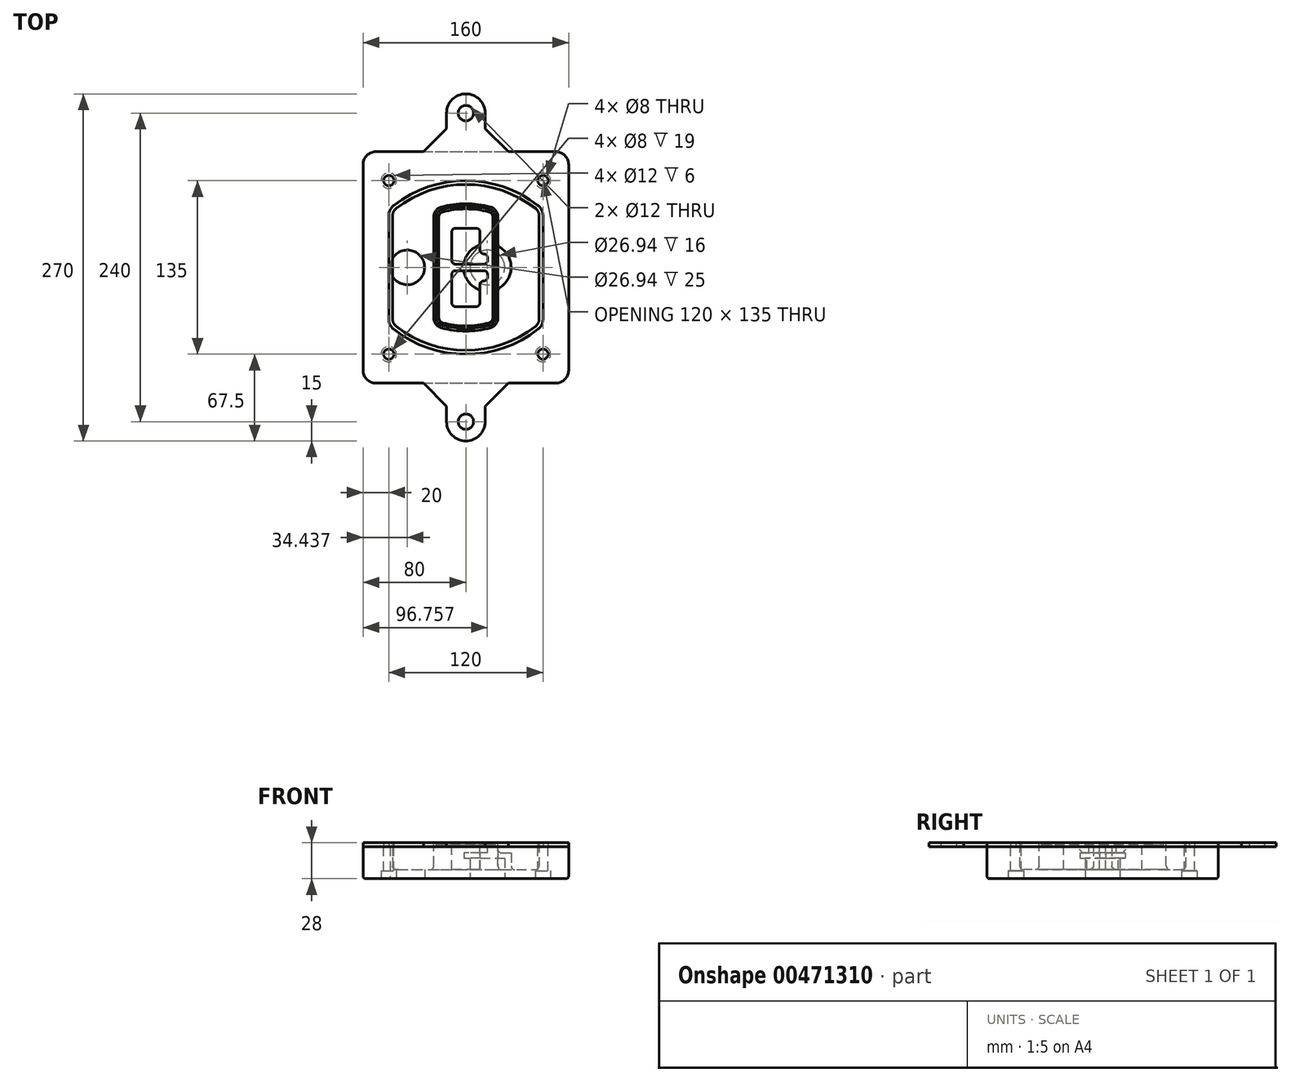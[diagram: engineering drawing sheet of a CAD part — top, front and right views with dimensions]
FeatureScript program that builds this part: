
annotation { "Feature Type Name" : "Feature", "Feature Type Description" : "" }
export const myFeature = defineFeature(function(context is Context, id is Id, definition is map)
    precondition{}
    {
        {
            var Q0;
            Q0=qCreatedBy(makeId("Top.planeOp"),FACE);
            var sketch = newSketch(context, id + "F0", { "sketchPlane" : qUnion([Q0])});
            skPoint(sketch, "E0.rect.middle", {"position": v(0, 0) * mm});
            skLineSegment(sketch, "E1.bottom", {"start": v(-70, -90) * mm, "end": v(70, -90) * mm});
            skLineSegment(sketch, "E1.top", {"start": v(-70, 90) * mm, "end": v(70, 90) * mm});
            skLineSegment(sketch, "E1.left", {"start": v(-80, -80) * mm, "end": v(-80, 80) * mm});
            skLineSegment(sketch, "E1.right", {"start": v(80, -80) * mm, "end": v(80, 80) * mm});
            skLineSegment(sketch, "E2", {"start": v(-80, 90) * mm, "end": v(80, -90) * mm, "construction": true});
            skLineSegment(sketch, "E3", {"start": v(80, 90) * mm, "end": v(-80, -90) * mm, "construction": true});
            skCircle(sketch, "E4", {"center": v(-60, 67.5) * mm, "radius": 4 * mm});
            skCircle(sketch, "E5", {"center": v(60, 67.5) * mm, "radius": 4 * mm});
            skCircle(sketch, "E6", {"center": v(60, -67.5) * mm, "radius": 4 * mm});
            skCircle(sketch, "E7", {"center": v(-60, -67.5) * mm, "radius": 4 * mm});
            skLineSegment(sketch, "E8", {"start": v(-60, 67.5) * mm, "end": v(60, 67.5) * mm, "construction": true});
            skLineSegment(sketch, "E9", {"start": v(60, 67.5) * mm, "end": v(60, -67.5) * mm, "construction": true});
            skLineSegment(sketch, "E10", {"start": v(60, -67.5) * mm, "end": v(-60, -67.5) * mm, "construction": true});
            skLineSegment(sketch, "E11", {"start": v(-60, -67.5) * mm, "end": v(-60, 67.5) * mm, "construction": true});
            skLineSegment(sketch, "E12", {"start": v(-60, 40.3) * mm, "end": v(-60, -40.3) * mm});
            skLineSegment(sketch, "E13", {"start": v(60, 40.3) * mm, "end": v(60, -40.3) * mm});
            skArc(sketch, "E14", {"start": v(56.15, 48.18) * mm, "mid": v(0, 67.5) * mm, "end": v(-56.15, 48.18) * mm});
            skArc(sketch, "E15", {"start": v(-56.15, -48.18) * mm, "mid": v(0, -67.5) * mm, "end": v(56.15, -48.18) * mm});
            skLineSegment(sketch, "E16", {"start": v(-60, 0) * mm, "end": v(60, 0) * mm, "construction": true});
            skPoint(sketch, "E17.visualSharp", {"position": v(-60, -45) * mm});
            skArc(sketch, "E17.filletArc", {"start": v(-60, -40.3) * mm, "mid": v(-58.99, -44.68) * mm, "end": v(-56.15, -48.18) * mm});
            skPoint(sketch, "E18.visualSharp", {"position": v(-60, 45) * mm});
            skArc(sketch, "E18.filletArc", {"start": v(-56.15, 48.18) * mm, "mid": v(-58.99, 44.68) * mm, "end": v(-60, 40.3) * mm});
            skPoint(sketch, "E19.visualSharp", {"position": v(60, 45) * mm});
            skArc(sketch, "E19.filletArc", {"start": v(60, 40.3) * mm, "mid": v(58.99, 44.68) * mm, "end": v(56.15, 48.18) * mm});
            skPoint(sketch, "E20.visualSharp", {"position": v(60, -45) * mm});
            skArc(sketch, "E20.filletArc", {"start": v(56.15, -48.18) * mm, "mid": v(58.99, -44.68) * mm, "end": v(60, -40.3) * mm});
            skPoint(sketch, "E21.visualSharp", {"position": v(-80, 90) * mm});
            skArc(sketch, "E21.filletArc", {"start": v(-70, 90) * mm, "mid": v(-77.07, 87.07) * mm, "end": v(-80, 80) * mm});
            skPoint(sketch, "E22.visualSharp", {"position": v(80, 90) * mm});
            skArc(sketch, "E22.filletArc", {"start": v(80, 80) * mm, "mid": v(77.07, 87.07) * mm, "end": v(70, 90) * mm});
            skPoint(sketch, "E23.visualSharp", {"position": v(80, -90) * mm});
            skArc(sketch, "E23.filletArc", {"start": v(70, -90) * mm, "mid": v(77.07, -87.07) * mm, "end": v(80, -80) * mm});
            skPoint(sketch, "E24.visualSharp", {"position": v(-80, -90) * mm});
            skArc(sketch, "E24.filletArc", {"start": v(-80, -80) * mm, "mid": v(-77.07, -87.07) * mm, "end": v(-70, -90) * mm});
            skArc(sketch, "E25.0", {"start": v(57, 40.3) * mm, "mid": v(56.3, 43.36) * mm, "end": v(54.3, 45.81) * mm});
            skLineSegment(sketch, "E25.1", {"start": v(57, 40.3) * mm, "end": v(57, -40.3) * mm});
            skArc(sketch, "E25.2", {"start": v(54.3, -45.81) * mm, "mid": v(56.3, -43.36) * mm, "end": v(57, -40.3) * mm});
            skArc(sketch, "E25.3", {"start": v(-54.3, -45.81) * mm, "mid": v(0, -64.5) * mm, "end": v(54.3, -45.81) * mm});
            skArc(sketch, "E25.4", {"start": v(-57, -40.3) * mm, "mid": v(-56.3, -43.36) * mm, "end": v(-54.3, -45.81) * mm});
            skArc(sketch, "E25.5", {"start": v(54.3, 45.81) * mm, "mid": v(0, 64.5) * mm, "end": v(-54.3, 45.81) * mm});
            skLineSegment(sketch, "E25.6", {"start": v(-57, 40.3) * mm, "end": v(-57, -40.3) * mm});
            skArc(sketch, "E25.7", {"start": v(-54.3, 45.81) * mm, "mid": v(-56.3, 43.36) * mm, "end": v(-57, 40.3) * mm});
            skArc(sketch, "E26.0", {"start": v(-58.62, 51.33) * mm, "mid": v(-62.58, 46.43) * mm, "end": v(-64, 40.3) * mm});
            skArc(sketch, "E26.1", {"start": v(58.62, 51.33) * mm, "mid": v(0, 71.5) * mm, "end": v(-58.62, 51.33) * mm});
            skArc(sketch, "E26.2", {"start": v(64, 40.3) * mm, "mid": v(62.58, 46.43) * mm, "end": v(58.62, 51.33) * mm});
            skLineSegment(sketch, "E26.3", {"start": v(64, 40.3) * mm, "end": v(64, -40.3) * mm});
            skArc(sketch, "E26.4", {"start": v(58.62, -51.33) * mm, "mid": v(62.58, -46.43) * mm, "end": v(64, -40.3) * mm});
            skLineSegment(sketch, "E26.5", {"start": v(-64, 40.3) * mm, "end": v(-64, -40.3) * mm});
            skArc(sketch, "E26.6", {"start": v(-58.62, -51.33) * mm, "mid": v(0, -71.5) * mm, "end": v(58.62, -51.33) * mm});
            skArc(sketch, "E26.7", {"start": v(-64, -40.3) * mm, "mid": v(-62.58, -46.43) * mm, "end": v(-58.62, -51.33) * mm});
            skSolve(sketch);
        }
        {
            var Q0;
            Q0=makeQuery(id+"F0.imprint","IMPRINT",FACE,{"disambiguationData":[TD([[makeQuery(id+"F0.imprint","IMPRINT",EDGE,{"derivedFrom":sQuery(id+"F0.wireOp",EDGE,"E1.bottom")}),1.0]])]});
            var Q1;
            Q1=makeQuery(id+"F0.imprint","IMPRINT",FACE,{"disambiguationData":[TD([[makeQuery(id+"F0.imprint","IMPRINT",EDGE,{"derivedFrom":sQuery(id+"F0.wireOp",EDGE,"E12")}),1.0]])]});
            var Q2;
            Q2=makeQuery(id+"F0.imprint","IMPRINT",FACE,{"disambiguationData":[TD([[makeQuery(id+"F0.imprint","IMPRINT",EDGE,{"derivedFrom":sQuery(id+"F0.wireOp",EDGE,"E25.0")}),1.0]])]});
            var Q3;
            Q3=makeQuery(id+"F0.imprint","IMPRINT",FACE,{"disambiguationData":[TD([[makeQuery(id+"F0.imprint","IMPRINT",EDGE,{"derivedFrom":sQuery(id+"F0.wireOp",EDGE,"E12")}),-1.0]])]});
            extrude(context, id + "F1", {"entities" : qUnion([Q0, Q1, Q2, Q3]), "oppositeDirection" : true, "depth" : 25 * mm});
        }
        {
            var Q0;
            Q0=makeQuery(id+"F0.imprint","IMPRINT",FACE,{"disambiguationData":[TD([[makeQuery(id+"F0.imprint","IMPRINT",EDGE,{"derivedFrom":sQuery(id+"F0.wireOp",EDGE,"E12")}),1.0]])]});
            extrude(context, id + "F2", {"entities" : qUnion([Q0]), "operationType" : NewBodyOperationType.ADD, "depth" : 3 * mm});
        }
        {
            var Q0;
            Q0=makeQuery(id+"F0.imprint","IMPRINT",FACE,{"disambiguationData":[TD([[makeQuery(id+"F0.imprint","IMPRINT",EDGE,{"derivedFrom":sQuery(id+"F0.wireOp",EDGE,"E25.0")}),1.0]])]});
            extrude(context, id + "F3", {"entities" : qUnion([Q0]), "operationType" : NewBodyOperationType.REMOVE, "oppositeDirection" : true, "depth" : 18 * mm});
        }
        {
            var Q0;
            Q0=makeQuery(id+"F2.opExtrude","CAP_FACE",FACE,{"disambiguationData":[OSD([sQuery(id+"F0.wireOp",EDGE,"E12"),sQuery(id+"F0.wireOp",EDGE,"E13"),sQuery(id+"F0.wireOp",EDGE,"E14"),sQuery(id+"F0.wireOp",EDGE,"E15"),sQuery(id+"F0.wireOp",EDGE,"E17.filletArc"),sQuery(id+"F0.wireOp",EDGE,"E18.filletArc"),sQuery(id+"F0.wireOp",EDGE,"E19.filletArc"),sQuery(id+"F0.wireOp",EDGE,"E20.filletArc"),sQuery(id+"F0.wireOp",EDGE,"E25.0"),sQuery(id+"F0.wireOp",EDGE,"E25.1"),sQuery(id+"F0.wireOp",EDGE,"E25.2"),sQuery(id+"F0.wireOp",EDGE,"E25.3"),sQuery(id+"F0.wireOp",EDGE,"E25.4"),sQuery(id+"F0.wireOp",EDGE,"E25.5"),sQuery(id+"F0.wireOp",EDGE,"E25.6"),sQuery(id+"F0.wireOp",EDGE,"E25.7")])],"isStart":false});
            var sketch = newSketch(context, id + "F4", { "sketchPlane" : qUnion([Q0])});
            skArc(sketch, "E27.0", {"start": v(-19.08, -46.97) * mm, "mid": v(0, -49.5) * mm, "end": v(19.08, -46.97) * mm});
            skArc(sketch, "E28.0", {"start": v(19.08, 46.97) * mm, "mid": v(0, 49.5) * mm, "end": v(-19.08, 46.97) * mm});
            skLineSegment(sketch, "E29", {"start": v(-25, 39.25) * mm, "end": v(-25, -39.25) * mm});
            skLineSegment(sketch, "E30", {"start": v(25, 39.25) * mm, "end": v(25, -39.25) * mm});
            skLineSegment(sketch, "E31", {"start": v(-25, 45.1) * mm, "end": v(25, 45.1) * mm, "construction": true});
            skLineSegment(sketch, "E32", {"start": v(-25, -45.1) * mm, "end": v(25, -45.1) * mm, "construction": true});
            skPoint(sketch, "E33.visualSharp", {"position": v(-25, 45.1) * mm});
            skArc(sketch, "E33.filletArc", {"start": v(-19.08, 46.97) * mm, "mid": v(-23.35, 44.11) * mm, "end": v(-25, 39.25) * mm});
            skPoint(sketch, "E34.visualSharp", {"position": v(25, 45.1) * mm});
            skArc(sketch, "E34.filletArc", {"start": v(25, 39.25) * mm, "mid": v(23.35, 44.11) * mm, "end": v(19.08, 46.97) * mm});
            skPoint(sketch, "E35.visualSharp", {"position": v(25, -45.1) * mm});
            skArc(sketch, "E35.filletArc", {"start": v(19.08, -46.97) * mm, "mid": v(23.35, -44.11) * mm, "end": v(25, -39.25) * mm});
            skPoint(sketch, "E36.visualSharp", {"position": v(-25, -45.1) * mm});
            skArc(sketch, "E36.filletArc", {"start": v(-25, -39.25) * mm, "mid": v(-23.35, -44.11) * mm, "end": v(-19.08, -46.97) * mm});
            skArc(sketch, "E37.0", {"start": v(54.3, 45.81) * mm, "mid": v(0, 64.5) * mm, "end": v(-54.3, 45.81) * mm});
            skArc(sketch, "E37.1", {"start": v(-54.3, 45.81) * mm, "mid": v(-56.3, 43.36) * mm, "end": v(-57, 40.3) * mm});
            skLineSegment(sketch, "E37.2", {"start": v(-57, 40.3) * mm, "end": v(-57, -40.3) * mm});
            skArc(sketch, "E37.3", {"start": v(-57, -40.3) * mm, "mid": v(-56.3, -43.36) * mm, "end": v(-54.3, -45.81) * mm});
            skArc(sketch, "E37.4", {"start": v(-54.3, -45.81) * mm, "mid": v(0, -64.5) * mm, "end": v(54.3, -45.81) * mm});
            skArc(sketch, "E37.5", {"start": v(54.3, -45.81) * mm, "mid": v(56.3, -43.36) * mm, "end": v(57, -40.3) * mm});
            skLineSegment(sketch, "E37.6", {"start": v(57, 40.3) * mm, "end": v(57, -40.3) * mm});
            skArc(sketch, "E37.7", {"start": v(57, 40.3) * mm, "mid": v(56.3, 43.36) * mm, "end": v(54.3, 45.81) * mm});
            skLineSegment(sketch, "E38.0", {"start": v(23, 39.25) * mm, "end": v(23, -39.25) * mm});
            skArc(sketch, "E38.1", {"start": v(18.56, -45.04) * mm, "mid": v(21.76, -42.9) * mm, "end": v(23, -39.25) * mm});
            skArc(sketch, "E38.2", {"start": v(-18.56, -45.04) * mm, "mid": v(0, -47.5) * mm, "end": v(18.56, -45.04) * mm});
            skArc(sketch, "E38.3", {"start": v(-23, -39.25) * mm, "mid": v(-21.76, -42.9) * mm, "end": v(-18.56, -45.04) * mm});
            skLineSegment(sketch, "E38.4", {"start": v(-23, 39.25) * mm, "end": v(-23, -39.25) * mm});
            skArc(sketch, "E38.5", {"start": v(23, 39.25) * mm, "mid": v(21.76, 42.9) * mm, "end": v(18.56, 45.04) * mm});
            skArc(sketch, "E38.6", {"start": v(-18.56, 45.04) * mm, "mid": v(-21.76, 42.9) * mm, "end": v(-23, 39.25) * mm});
            skArc(sketch, "E38.7", {"start": v(18.56, 45.04) * mm, "mid": v(0, 47.5) * mm, "end": v(-18.56, 45.04) * mm});
            skArc(sketch, "E39.0", {"start": v(21, 39.25) * mm, "mid": v(20.18, 41.68) * mm, "end": v(18.04, 43.1) * mm});
            skLineSegment(sketch, "E39.1", {"start": v(21, 39.25) * mm, "end": v(21, -39.25) * mm});
            skArc(sketch, "E39.2", {"start": v(18.04, -43.1) * mm, "mid": v(20.18, -41.68) * mm, "end": v(21, -39.25) * mm});
            skArc(sketch, "E39.3", {"start": v(-18.04, -43.1) * mm, "mid": v(0, -45.5) * mm, "end": v(18.04, -43.1) * mm});
            skArc(sketch, "E39.4", {"start": v(-21, -39.25) * mm, "mid": v(-20.18, -41.68) * mm, "end": v(-18.04, -43.1) * mm});
            skArc(sketch, "E39.5", {"start": v(18.04, 43.1) * mm, "mid": v(0, 45.5) * mm, "end": v(-18.04, 43.1) * mm});
            skLineSegment(sketch, "E39.6", {"start": v(-21, 39.25) * mm, "end": v(-21, -39.25) * mm});
            skArc(sketch, "E39.7", {"start": v(-18.04, 43.1) * mm, "mid": v(-20.18, 41.68) * mm, "end": v(-21, 39.25) * mm});
            skLineSegment(sketch, "E40", {"start": v(-25, 0) * mm, "end": v(25, 0) * mm, "construction": true});
            skLineSegment(sketch, "E41", {"start": v(-11, 5.5) * mm, "end": v(-11, 27.5) * mm});
            skLineSegment(sketch, "E42", {"start": v(-8, 30.5) * mm, "end": v(8, 30.5) * mm});
            skLineSegment(sketch, "E43", {"start": v(11, 27.5) * mm, "end": v(11, 13.5) * mm});
            skLineSegment(sketch, "E44", {"start": v(14, 10.5) * mm, "end": v(14, 10.5) * mm});
            skLineSegment(sketch, "E45", {"start": v(17, 7.5) * mm, "end": v(17, 5.5) * mm});
            skLineSegment(sketch, "E46", {"start": v(14, 2.5) * mm, "end": v(-8, 2.5) * mm});
            skPoint(sketch, "E47.visualSharp", {"position": v(-11, 30.5) * mm});
            skArc(sketch, "E47.filletArc", {"start": v(-8, 30.5) * mm, "mid": v(-10.12, 29.62) * mm, "end": v(-11, 27.5) * mm});
            skPoint(sketch, "E48.visualSharp", {"position": v(11, 30.5) * mm});
            skArc(sketch, "E48.filletArc", {"start": v(11, 27.5) * mm, "mid": v(10.12, 29.62) * mm, "end": v(8, 30.5) * mm});
            skPoint(sketch, "E49.visualSharp", {"position": v(11, 10.5) * mm});
            skArc(sketch, "E49.filletArc", {"start": v(11, 13.5) * mm, "mid": v(11.88, 11.38) * mm, "end": v(14, 10.5) * mm});
            skPoint(sketch, "E50.visualSharp", {"position": v(17, 10.5) * mm});
            skArc(sketch, "E50.filletArc", {"start": v(17, 7.5) * mm, "mid": v(16.12, 9.62) * mm, "end": v(14, 10.5) * mm});
            skPoint(sketch, "E51.visualSharp", {"position": v(17, 2.5) * mm});
            skArc(sketch, "E51.filletArc", {"start": v(14, 2.5) * mm, "mid": v(16.12, 3.38) * mm, "end": v(17, 5.5) * mm});
            skPoint(sketch, "E52.visualSharp", {"position": v(-11, 2.5) * mm});
            skArc(sketch, "E52.filletArc", {"start": v(-11, 5.5) * mm, "mid": v(-10.12, 3.38) * mm, "end": v(-8, 2.5) * mm});
            skLineSegment(sketch, "E53.0.MirrorCS", {"start": v(14, -2.5) * mm, "end": v(-8, -2.5) * mm});
            skArc(sketch, "E54.0.MirrorCS", {"start": v(-11, -5.5) * mm, "mid": v(-10.12, -3.38) * mm, "end": v(-8, -2.5) * mm});
            skLineSegment(sketch, "E55.0.MirrorCS", {"start": v(-11, -5.5) * mm, "end": v(-11, -27.5) * mm});
            skArc(sketch, "E56.0.MirrorCS", {"start": v(-8, -30.5) * mm, "mid": v(-10.12, -29.62) * mm, "end": v(-11, -27.5) * mm});
            skLineSegment(sketch, "E57.0.MirrorCS", {"start": v(-8, -30.5) * mm, "end": v(8, -30.5) * mm});
            skArc(sketch, "E58.0.MirrorCS", {"start": v(11, -27.5) * mm, "mid": v(10.12, -29.62) * mm, "end": v(8, -30.5) * mm});
            skLineSegment(sketch, "E59.0.MirrorCS", {"start": v(11, -27.5) * mm, "end": v(11, -13.5) * mm});
            skArc(sketch, "E60.0.MirrorCS", {"start": v(11, -13.5) * mm, "mid": v(11.88, -11.38) * mm, "end": v(14, -10.5) * mm});
            skArc(sketch, "E61.0.MirrorCS", {"start": v(17, -7.5) * mm, "mid": v(16.12, -9.62) * mm, "end": v(14, -10.5) * mm});
            skLineSegment(sketch, "E62.0.MirrorCS", {"start": v(17, -7.5) * mm, "end": v(17, -5.5) * mm});
            skArc(sketch, "E63.0.MirrorCS", {"start": v(14, -2.5) * mm, "mid": v(16.12, -3.38) * mm, "end": v(17, -5.5) * mm});
            skSolve(sketch);
        }
        {
            var Q0;
            Q0=makeQuery(id+"F4.imprint","IMPRINT",FACE,{"disambiguationData":[TD([[makeQuery(id+"F4.imprint","IMPRINT",EDGE,{"derivedFrom":sQuery(id+"F4.wireOp",EDGE,"E27.0")}),1.0]])]});
            var Q1;
            Q1=makeQuery(id+"F4.imprint","IMPRINT",FACE,{"disambiguationData":[TD([[makeQuery(id+"F4.imprint","IMPRINT",EDGE,{"derivedFrom":sQuery(id+"F4.wireOp",EDGE,"E38.0")}),-1.0]])]});
            var Q2;
            Q2=makeQuery(id+"F4.imprint","IMPRINT",FACE,{"disambiguationData":[TD([[makeQuery(id+"F4.imprint","IMPRINT",EDGE,{"derivedFrom":sQuery(id+"F4.wireOp",EDGE,"E39.0")}),1.0]])]});
            extrude(context, id + "F5", {"entities" : qUnion([Q0, Q1, Q2]), "operationType" : NewBodyOperationType.ADD, "endBound" : BoundingType.UP_TO_NEXT, "oppositeDirection" : true, "depth" : 25 * mm});
        }
        {
            var Q0;
            Q0=makeQuery(id+"F4.imprint","IMPRINT",FACE,{"disambiguationData":[TD([[makeQuery(id+"F4.imprint","IMPRINT",EDGE,{"derivedFrom":sQuery(id+"F4.wireOp",EDGE,"E38.0")}),-1.0]])]});
            extrude(context, id + "F6", {"entities" : qUnion([Q0]), "operationType" : NewBodyOperationType.REMOVE, "oppositeDirection" : true, "depth" : 2 * mm});
        }
        {
            var Q0;
            Q0=makeQuery(id+"F1.opExtrude","CAP_FACE",FACE,{"disambiguationData":[OSD([sQuery(id+"F0.wireOp",EDGE,"E1.bottom"),sQuery(id+"F0.wireOp",EDGE,"E1.top"),sQuery(id+"F0.wireOp",EDGE,"E1.left"),sQuery(id+"F0.wireOp",EDGE,"E1.right"),sQuery(id+"F0.wireOp",EDGE,"E4"),sQuery(id+"F0.wireOp",EDGE,"E5"),sQuery(id+"F0.wireOp",EDGE,"E6"),sQuery(id+"F0.wireOp",EDGE,"E7"),sQuery(id+"F0.wireOp",EDGE,"E21.filletArc"),sQuery(id+"F0.wireOp",EDGE,"E22.filletArc"),sQuery(id+"F0.wireOp",EDGE,"E23.filletArc"),sQuery(id+"F0.wireOp",EDGE,"E24.filletArc")])],"isStart":false});
            var sketch = newSketch(context, id + "F7", { "sketchPlane" : qUnion([Q0])});
            skCircle(sketch, "E64", {"center": v(16.76, 0) * mm, "radius": 13.47 * mm});
            skCircle(sketch, "E65", {"center": v(-45.56, 0) * mm, "radius": 13.47 * mm});
            skLineSegment(sketch, "E66", {"start": v(80, 0) * mm, "end": v(-80, 0) * mm});
            skCircle(sketch, "E67", {"center": v(16.76, 0) * mm, "radius": 18.47 * mm});
            skCircle(sketch, "E68", {"center": v(60, -67.5) * mm, "radius": 6 * mm});
            skCircle(sketch, "E69", {"center": v(-60, -67.5) * mm, "radius": 6 * mm});
            skCircle(sketch, "E70", {"center": v(-60, 67.5) * mm, "radius": 6 * mm});
            skCircle(sketch, "E71", {"center": v(60, 67.5) * mm, "radius": 6 * mm});
            skSolve(sketch);
        }
        {
            var Q0;
            {var subQ1=sQuery(id+"F7.wireOp",EDGE,"E66");var subQ4=sQuery(id+"F7.wireOp",EDGE,"E64");var subQ6=makeQuery(id+"F7.imprint","INTERSECT",VERTEX,{"disambiguationData":[OD(0.0)],"derivedFrom":[subQ4,subQ1]});Q0=makeQuery(id+"F7.imprint","IMPRINT",FACE,{"disambiguationData":[TD([[makeQuery(id+"F7.imprint","IMPRINT",EDGE,{"disambiguationData":[TD([[subQ6,-1.0]])],"derivedFrom":subQ4}),-1.0]])]});}
            var Q1;
            {var subQ0=sQuery(id+"F7.wireOp",EDGE,"E66");var subQ1=sQuery(id+"F7.wireOp",EDGE,"E64");var subQ3=makeQuery(id+"F7.imprint","INTERSECT",VERTEX,{"disambiguationData":[OD(0.0)],"derivedFrom":[subQ1,subQ0]});Q1=makeQuery(id+"F7.imprint","IMPRINT",FACE,{"disambiguationData":[TD([[makeQuery(id+"F7.imprint","IMPRINT",EDGE,{"disambiguationData":[TD([[subQ3,-1.0]])],"derivedFrom":subQ1}),1.0]])]});}
            var Q2;
            {var subQ0=sQuery(id+"F7.wireOp",EDGE,"E66");var subQ1=sQuery(id+"F7.wireOp",EDGE,"E64");var subQ3=makeQuery(id+"F7.imprint","INTERSECT",VERTEX,{"disambiguationData":[OD(0.0)],"derivedFrom":[subQ1,subQ0]});Q2=makeQuery(id+"F7.imprint","IMPRINT",FACE,{"disambiguationData":[TD([[makeQuery(id+"F7.imprint","IMPRINT",EDGE,{"disambiguationData":[TD([[subQ3,1.0]])],"derivedFrom":subQ1}),1.0]])]});}
            var Q3;
            {var subQ1=sQuery(id+"F7.wireOp",EDGE,"E66");var subQ4=sQuery(id+"F7.wireOp",EDGE,"E64");var subQ6=makeQuery(id+"F7.imprint","INTERSECT",VERTEX,{"disambiguationData":[OD(0.0)],"derivedFrom":[subQ4,subQ1]});Q3=makeQuery(id+"F7.imprint","IMPRINT",FACE,{"disambiguationData":[TD([[makeQuery(id+"F7.imprint","IMPRINT",EDGE,{"disambiguationData":[TD([[subQ6,1.0]])],"derivedFrom":subQ4}),-1.0]])]});}
            extrude(context, id + "F8", {"entities" : qUnion([Q0, Q1, Q2, Q3]), "operationType" : NewBodyOperationType.ADD, "oppositeDirection" : true, "depth" : 20 * mm});
        }
        {
            var Q0;
            {var subQ0=sQuery(id+"F7.wireOp",EDGE,"E66");var subQ1=sQuery(id+"F7.wireOp",EDGE,"E64");var subQ3=makeQuery(id+"F7.imprint","INTERSECT",VERTEX,{"disambiguationData":[OD(0.0)],"derivedFrom":[subQ1,subQ0]});Q0=makeQuery(id+"F7.imprint","IMPRINT",FACE,{"disambiguationData":[TD([[makeQuery(id+"F7.imprint","IMPRINT",EDGE,{"disambiguationData":[TD([[subQ3,-1.0]])],"derivedFrom":subQ1}),1.0]])]});}
            var Q1;
            {var subQ0=sQuery(id+"F7.wireOp",EDGE,"E66");var subQ1=sQuery(id+"F7.wireOp",EDGE,"E64");var subQ3=makeQuery(id+"F7.imprint","INTERSECT",VERTEX,{"disambiguationData":[OD(0.0)],"derivedFrom":[subQ1,subQ0]});Q1=makeQuery(id+"F7.imprint","IMPRINT",FACE,{"disambiguationData":[TD([[makeQuery(id+"F7.imprint","IMPRINT",EDGE,{"disambiguationData":[TD([[subQ3,1.0]])],"derivedFrom":subQ1}),1.0]])]});}
            extrude(context, id + "F9", {"entities" : qUnion([Q0, Q1]), "operationType" : NewBodyOperationType.REMOVE, "oppositeDirection" : true, "depth" : 16 * mm});
        }
        {
            var Q0;
            {var subQ0=sQuery(id+"F7.wireOp",EDGE,"E66");var subQ1=sQuery(id+"F7.wireOp",EDGE,"E65");var subQ3=makeQuery(id+"F7.imprint","INTERSECT",VERTEX,{"disambiguationData":[OD(0.0)],"derivedFrom":[subQ1,subQ0]});Q0=makeQuery(id+"F7.imprint","IMPRINT",FACE,{"disambiguationData":[TD([[makeQuery(id+"F7.imprint","IMPRINT",EDGE,{"disambiguationData":[TD([[subQ3,-1.0]])],"derivedFrom":subQ1}),1.0]])]});}
            var Q1;
            {var subQ0=sQuery(id+"F7.wireOp",EDGE,"E66");var subQ1=sQuery(id+"F7.wireOp",EDGE,"E65");var subQ3=makeQuery(id+"F7.imprint","INTERSECT",VERTEX,{"disambiguationData":[OD(0.0)],"derivedFrom":[subQ1,subQ0]});Q1=makeQuery(id+"F7.imprint","IMPRINT",FACE,{"disambiguationData":[TD([[makeQuery(id+"F7.imprint","IMPRINT",EDGE,{"disambiguationData":[TD([[subQ3,1.0]])],"derivedFrom":subQ1}),1.0]])]});}
            extrude(context, id + "F10", {"entities" : qUnion([Q0, Q1]), "operationType" : NewBodyOperationType.REMOVE, "oppositeDirection" : true, "depth" : 25 * mm});
        }
        {
            var Q0;
            Q0=makeQuery(id+"F7.imprint","IMPRINT",FACE,{"disambiguationData":[TD([[makeQuery(id+"F7.imprint","IMPRINT",EDGE,{"derivedFrom":sQuery(id+"F7.wireOp",EDGE,"E68")}),1.0]])]});
            var Q1;
            Q1=makeQuery(id+"F7.imprint","IMPRINT",FACE,{"disambiguationData":[TD([[makeQuery(id+"F7.imprint","IMPRINT",EDGE,{"derivedFrom":makeQuery(id+"F1.opExtrude","CAP_EDGE",EDGE,{"disambiguationData":[OSD([sQuery(id+"F0.wireOp",EDGE,"E5")])],"isStart":false})}),-1.0]])]});
            var Q2;
            Q2=makeQuery(id+"F7.imprint","IMPRINT",FACE,{"disambiguationData":[TD([[makeQuery(id+"F7.imprint","IMPRINT",EDGE,{"derivedFrom":sQuery(id+"F7.wireOp",EDGE,"E69")}),1.0]])]});
            var Q3;
            Q3=makeQuery(id+"F7.imprint","IMPRINT",FACE,{"disambiguationData":[TD([[makeQuery(id+"F7.imprint","IMPRINT",EDGE,{"derivedFrom":makeQuery(id+"F1.opExtrude","CAP_EDGE",EDGE,{"disambiguationData":[OSD([sQuery(id+"F0.wireOp",EDGE,"E4")])],"isStart":false})}),-1.0]])]});
            var Q4;
            Q4=makeQuery(id+"F7.imprint","IMPRINT",FACE,{"disambiguationData":[TD([[makeQuery(id+"F7.imprint","IMPRINT",EDGE,{"derivedFrom":sQuery(id+"F7.wireOp",EDGE,"E70")}),1.0]])]});
            var Q5;
            Q5=makeQuery(id+"F7.imprint","IMPRINT",FACE,{"disambiguationData":[TD([[makeQuery(id+"F7.imprint","IMPRINT",EDGE,{"derivedFrom":makeQuery(id+"F1.opExtrude","CAP_EDGE",EDGE,{"disambiguationData":[OSD([sQuery(id+"F0.wireOp",EDGE,"E7")])],"isStart":false})}),-1.0]])]});
            var Q6;
            Q6=makeQuery(id+"F7.imprint","IMPRINT",FACE,{"disambiguationData":[TD([[makeQuery(id+"F7.imprint","IMPRINT",EDGE,{"derivedFrom":sQuery(id+"F7.wireOp",EDGE,"E71")}),1.0]])]});
            var Q7;
            Q7=makeQuery(id+"F7.imprint","IMPRINT",FACE,{"disambiguationData":[TD([[makeQuery(id+"F7.imprint","IMPRINT",EDGE,{"derivedFrom":makeQuery(id+"F1.opExtrude","CAP_EDGE",EDGE,{"disambiguationData":[OSD([sQuery(id+"F0.wireOp",EDGE,"E6")])],"isStart":false})}),-1.0]])]});
            extrude(context, id + "F11", {"entities" : qUnion([Q0, Q1, Q2, Q3, Q4, Q5, Q6, Q7]), "operationType" : NewBodyOperationType.REMOVE, "oppositeDirection" : true, "depth" : 6 * mm});
        }
        {
            var Q0;
            Q0=makeQuery(id+"F9.boolean.opBoolean","COPY",FACE,{"derivedFrom":makeQuery(id+"F9.opExtrude","CAP_FACE",FACE,{"disambiguationData":[OSD([sQuery(id+"F7.wireOp",EDGE,"E64")])],"isStart":false})});
            var sketch = newSketch(context, id + "F12", { "sketchPlane" : qUnion([Q0])});
            skArc(sketch, "E72.0", {"start": v(11, 17.55) * mm, "mid": v(2.57, 11.82) * mm, "end": v(-1.54, 2.5) * mm});
            skArc(sketch, "E72.1", {"start": v(-1.54, -2.5) * mm, "mid": v(2.57, -11.82) * mm, "end": v(11, -17.55) * mm});
            skLineSegment(sketch, "E73", {"start": v(-1.54, -2.5) * mm, "end": v(14, -2.5) * mm});
            skLineSegment(sketch, "E74.0", {"start": v(14, 2.5) * mm, "end": v(-1.54, 2.5) * mm});
            skArc(sketch, "E74.1", {"start": v(14, 2.5) * mm, "mid": v(16.12, 3.38) * mm, "end": v(17, 5.5) * mm});
            skLineSegment(sketch, "E74.2", {"start": v(17, 7.5) * mm, "end": v(17, 5.5) * mm});
            skArc(sketch, "E74.3", {"start": v(17, 7.5) * mm, "mid": v(16.12, 9.62) * mm, "end": v(14, 10.5) * mm});
            skArc(sketch, "E74.4", {"start": v(11, 13.5) * mm, "mid": v(11.88, 11.38) * mm, "end": v(14, 10.5) * mm});
            skLineSegment(sketch, "E74.5", {"start": v(11, 17.55) * mm, "end": v(11, 13.5) * mm});
            skLineSegment(sketch, "E74.7", {"start": v(14, -2.5) * mm, "end": v(-1.54, -2.5) * mm});
            skArc(sketch, "E74.8", {"start": v(14, -2.5) * mm, "mid": v(16.12, -3.38) * mm, "end": v(17, -5.5) * mm});
            skLineSegment(sketch, "E74.9", {"start": v(17, -7.5) * mm, "end": v(17, -5.5) * mm});
            skArc(sketch, "E74.10", {"start": v(17, -7.5) * mm, "mid": v(16.12, -9.62) * mm, "end": v(14, -10.5) * mm});
            skArc(sketch, "E74.11", {"start": v(11, -13.5) * mm, "mid": v(11.88, -11.38) * mm, "end": v(14, -10.5) * mm});
            skLineSegment(sketch, "E74.12", {"start": v(11, -17.55) * mm, "end": v(11, -13.5) * mm});
            skPoint(sketch, "E75.orphan", {"position": v(11, -27.5) * mm});
            skPoint(sketch, "E76.orphan", {"position": v(-8, -2.5) * mm});
            skPoint(sketch, "E77.orphan", {"position": v(-8, 2.5) * mm});
            skPoint(sketch, "E78.orphan", {"position": v(11, 27.5) * mm});
            skSolve(sketch);
        }
        {
            var Q0;
            {var subQ7=sQuery(id+"F12.wireOp",EDGE,"E72.0");var subQ14=sQuery(id+"F12.wireOp",EDGE,"E72.1");var subQ16=sQuery(id+"F12.wireOp",EDGE,"E74.1");var subQ18=sQuery(id+"F12.wireOp",EDGE,"E74.8");Q0=qUnion([makeQuery(id+"F12.imprint","IMPRINT",FACE,{"disambiguationData":[TD([[makeQuery(id+"F12.imprint","IMPRINT",EDGE,{"derivedFrom":subQ7}),1.0]])]}),makeQuery(id+"F12.imprint","IMPRINT",FACE,{"disambiguationData":[TD([[makeQuery(id+"F12.imprint","IMPRINT",EDGE,{"derivedFrom":subQ14}),1.0]])]}),makeQuery(id+"F12.imprint","IMPRINT",FACE,{"disambiguationData":[TD([[makeQuery(id+"F12.imprint","IMPRINT",EDGE,{"derivedFrom":subQ16}),1.0]])]}),makeQuery(id+"F12.imprint","IMPRINT",FACE,{"disambiguationData":[TD([[makeQuery(id+"F12.imprint","IMPRINT",EDGE,{"derivedFrom":subQ18}),-1.0]])]})]);}
            var Q1;
            Q1=makeQuery(id+"F5.boolean.opBoolean","SPLIT",FACE,{"disambiguationData":[TD([makeQuery(id+"F5.opExtrude","SWEPT_FACE",FACE,{"disambiguationData":[OSD([sQuery(id+"F4.wireOp",EDGE,"E41")])]})])],"derivedFrom":makeQuery(id+"F3.boolean.opBoolean","COPY",FACE,{"derivedFrom":makeQuery(id+"F3.opExtrude","CAP_FACE",FACE,{"disambiguationData":[OSD([sQuery(id+"F0.wireOp",EDGE,"E25.0"),sQuery(id+"F0.wireOp",EDGE,"E25.1"),sQuery(id+"F0.wireOp",EDGE,"E25.2"),sQuery(id+"F0.wireOp",EDGE,"E25.3"),sQuery(id+"F0.wireOp",EDGE,"E25.4"),sQuery(id+"F0.wireOp",EDGE,"E25.5"),sQuery(id+"F0.wireOp",EDGE,"E25.6"),sQuery(id+"F0.wireOp",EDGE,"E25.7")])],"isStart":false})})});
            extrude(context, id + "F13", {"entities" : qUnion([Q0]), "operationType" : NewBodyOperationType.REMOVE, "endBound" : BoundingType.UP_TO_SURFACE, "endBoundEntityFace" : qUnion([Q1]), "depth" : 25 * mm});
        }
        {
            var Q0;
            Q0=makeQuery(id+"F3.boolean.opBoolean","COPY",EDGE,{"derivedFrom":makeQuery(id+"F3.opExtrude","CAP_EDGE",EDGE,{"disambiguationData":[OSD([sQuery(id+"F0.wireOp",EDGE,"E25.6")])],"isStart":false})});
            var Q1;
            Q1=makeQuery(id+"F8.boolean.opBoolean","INTERSECT",EDGE,{"derivedFrom":[makeQuery(id+"F5.opExtrude","SWEPT_FACE",FACE,{"disambiguationData":[OSD([sQuery(id+"F4.wireOp",EDGE,"E30")])]}),makeQuery(id+"F8.opExtrude","CAP_FACE",FACE,{"disambiguationData":[OSD([sQuery(id+"F7.wireOp",EDGE,"E67")])],"isStart":false})]});
            var Q2;
            Q2=makeQuery(id+"F8.boolean.opBoolean","INTERSECT",EDGE,{"disambiguationData":[OD(1.0)],"derivedFrom":[makeQuery(id+"F5.opExtrude","SWEPT_FACE",FACE,{"disambiguationData":[OSD([sQuery(id+"F4.wireOp",EDGE,"E30")])]}),makeQuery(id+"F8.opExtrude","SWEPT_FACE",FACE,{"disambiguationData":[OSD([sQuery(id+"F7.wireOp",EDGE,"E67")])]})]});
            var Q3;
            {var subQ0=sQuery(id+"F4.wireOp",EDGE,"E30");Q3=makeQuery(id+"F8.boolean.opBoolean","SPLIT",EDGE,{"disambiguationData":[TD([makeQuery(id+"F5.opExtrude","SWEPT_FACE",FACE,{"disambiguationData":[OSD([sQuery(id+"F4.wireOp",EDGE,"E35.filletArc")])]})])],"derivedFrom":makeQuery(id+"F5.opExtrude","CAP_EDGE",EDGE,{"disambiguationData":[OSD([subQ0])],"isStart":false})});}
            var Q4;
            {var subQ0=sQuery(id+"F0.wireOp",EDGE,"E25.7");var subQ1=sQuery(id+"F0.wireOp",EDGE,"E25.1");var subQ2=sQuery(id+"F0.wireOp",EDGE,"E25.6");var subQ3=sQuery(id+"F0.wireOp",EDGE,"E25.5");var subQ4=sQuery(id+"F0.wireOp",EDGE,"E25.4");var subQ5=sQuery(id+"F0.wireOp",EDGE,"E25.0");var subQ6=sQuery(id+"F0.wireOp",EDGE,"E25.2");var subQ7=sQuery(id+"F0.wireOp",EDGE,"E25.3");Q4=makeQuery(id+"F8.boolean.opBoolean","INTERSECT",EDGE,{"derivedFrom":[makeQuery(id+"F5.boolean.opBoolean","SPLIT",FACE,{"disambiguationData":[TD([makeQuery(id+"F2.opExtrude","SWEPT_FACE",FACE,{"disambiguationData":[OSD([subQ5])]})])],"derivedFrom":makeQuery(id+"F3.boolean.opBoolean","COPY",FACE,{"derivedFrom":makeQuery(id+"F3.opExtrude","CAP_FACE",FACE,{"disambiguationData":[OSD([subQ5,subQ1,subQ6,subQ7,subQ4,subQ3,subQ2,subQ0])],"isStart":false})})}),makeQuery(id+"F8.opExtrude","SWEPT_FACE",FACE,{"disambiguationData":[OSD([sQuery(id+"F7.wireOp",EDGE,"E67")])]})]});}
            var Q5;
            Q5=makeQuery(id+"F8.boolean.opBoolean","INTERSECT",EDGE,{"disambiguationData":[OD(0.0)],"derivedFrom":[makeQuery(id+"F5.opExtrude","SWEPT_FACE",FACE,{"disambiguationData":[OSD([sQuery(id+"F4.wireOp",EDGE,"E30")])]}),makeQuery(id+"F8.opExtrude","SWEPT_FACE",FACE,{"disambiguationData":[OSD([sQuery(id+"F7.wireOp",EDGE,"E67")])]})]});
            fillet(context, id + "F14", {"entities" : qUnion([Q0, Q1, Q2, Q3, Q4, Q5]), "radius" : 3 * mm, "tangentPropagation" : true, "allowEdgeOverflow" : false});
        }
        {
            var Q0;
            Q0=makeQuery(id+"F1.opExtrude","CAP_EDGE",EDGE,{"disambiguationData":[OSD([sQuery(id+"F0.wireOp",EDGE,"E1.bottom")])],"isStart":false});
            fillet(context, id + "F15", {"entities" : qUnion([Q0]), "radius" : 2 * mm, "tangentPropagation" : true, "allowEdgeOverflow" : false});
        }
        {
            var Q0;
            {var subQ0=sQuery(id+"F0.wireOp",EDGE,"E21.filletArc");var subQ1=sQuery(id+"F0.wireOp",EDGE,"E7");var subQ2=sQuery(id+"F0.wireOp",EDGE,"E6");var subQ3=sQuery(id+"F0.wireOp",EDGE,"E5");var subQ4=sQuery(id+"F0.wireOp",EDGE,"E4");var subQ5=sQuery(id+"F0.wireOp",EDGE,"E22.filletArc");var subQ6=sQuery(id+"F0.wireOp",EDGE,"E1.bottom");var subQ7=sQuery(id+"F0.wireOp",EDGE,"E1.right");var subQ8=sQuery(id+"F0.wireOp",EDGE,"E1.top");var subQ9=sQuery(id+"F0.wireOp",EDGE,"E1.left");var subQ10=sQuery(id+"F0.wireOp",EDGE,"E23.filletArc");var subQ11=sQuery(id+"F0.wireOp",EDGE,"E24.filletArc");Q0=makeQuery(id+"F2.boolean.opBoolean","SPLIT",FACE,{"disambiguationData":[TD([makeQuery(id+"F1.opExtrude","SWEPT_FACE",FACE,{"disambiguationData":[OSD([subQ6])]})])],"derivedFrom":makeQuery(id+"F1.opExtrude","CAP_FACE",FACE,{"disambiguationData":[OSD([subQ6,subQ8,subQ9,subQ7,subQ4,subQ3,subQ2,subQ1,subQ0,subQ5,subQ10,subQ11])],"isStart":true})});}
            var sketch = newSketch(context, id + "F16", { "sketchPlane" : qUnion([Q0])});
            skPoint(sketch, "E79.endSnap0", {"position": v(0, 90) * mm});
            skCircle(sketch, "E80", {"center": v(0, 120) * mm, "radius": 6 * mm});
            skArc(sketch, "E81", {"start": v(-15, 120) * mm, "mid": v(0, 135) * mm, "end": v(15, 120) * mm});
            skLineSegment(sketch, "E82", {"start": v(-15, 120) * mm, "end": v(-15, 108) * mm});
            skLineSegment(sketch, "E83", {"start": v(15, 120) * mm, "end": v(15, 108) * mm});
            skLineSegment(sketch, "E84", {"start": v(15, 108) * mm, "end": v(33, 90) * mm});
            skLineSegment(sketch, "E85", {"start": v(-15, 108) * mm, "end": v(-33, 90) * mm});
            skCircle(sketch, "E86", {"center": v(0, -120) * mm, "radius": 6 * mm});
            skArc(sketch, "E87", {"start": v(-15, -120) * mm, "mid": v(0, -135) * mm, "end": v(15, -120) * mm});
            skLineSegment(sketch, "E88", {"start": v(-15, -120) * mm, "end": v(-15, -108) * mm});
            skLineSegment(sketch, "E89", {"start": v(15, -120) * mm, "end": v(15, -108) * mm});
            skLineSegment(sketch, "E90", {"start": v(-33, -90) * mm, "end": v(-15, -108) * mm});
            skLineSegment(sketch, "E91", {"start": v(15, -108) * mm, "end": v(33, -90) * mm});
            skLineSegment(sketch, "E92", {"start": v(0, 90) * mm, "end": v(0, 120) * mm, "construction": true});
            skLineSegment(sketch, "E93", {"start": v(0, -90) * mm, "end": v(0, -120) * mm, "construction": true});
            skSolve(sketch);
        }
        {
            var Q0;
            Q0=makeQuery(id+"F16.imprint","IMPRINT",FACE,{"disambiguationData":[TD([[makeQuery(id+"F16.imprint","IMPRINT",EDGE,{"derivedFrom":sQuery(id+"F16.wireOp",EDGE,"E86")}),-1.0]])]});
            var Q1;
            Q1=makeQuery(id+"F16.imprint","IMPRINT",FACE,{"disambiguationData":[TD([[makeQuery(id+"F16.imprint","IMPRINT",EDGE,{"derivedFrom":sQuery(id+"F16.wireOp",EDGE,"E80")}),-1.0]])]});
            var Q2;
            Q2=makeQuery(id+"F16.imprint","IMPRINT",FACE,{"disambiguationData":[TD([[makeQuery(id+"F16.imprint","IMPRINT",EDGE,{"derivedFrom":makeQuery(id+"F1.opExtrude","CAP_EDGE",EDGE,{"disambiguationData":[OSD([sQuery(id+"F0.wireOp",EDGE,"E1.left")])],"isStart":true})}),-1.0]])]});
            var Q3;
            Q3=makeQuery(id+"F2.opExtrude","CAP_FACE",FACE,{"disambiguationData":[OSD([sQuery(id+"F0.wireOp",EDGE,"E12"),sQuery(id+"F0.wireOp",EDGE,"E13"),sQuery(id+"F0.wireOp",EDGE,"E14"),sQuery(id+"F0.wireOp",EDGE,"E15"),sQuery(id+"F0.wireOp",EDGE,"E17.filletArc"),sQuery(id+"F0.wireOp",EDGE,"E18.filletArc"),sQuery(id+"F0.wireOp",EDGE,"E19.filletArc"),sQuery(id+"F0.wireOp",EDGE,"E20.filletArc"),sQuery(id+"F0.wireOp",EDGE,"E25.0"),sQuery(id+"F0.wireOp",EDGE,"E25.1"),sQuery(id+"F0.wireOp",EDGE,"E25.2"),sQuery(id+"F0.wireOp",EDGE,"E25.3"),sQuery(id+"F0.wireOp",EDGE,"E25.4"),sQuery(id+"F0.wireOp",EDGE,"E25.5"),sQuery(id+"F0.wireOp",EDGE,"E25.6"),sQuery(id+"F0.wireOp",EDGE,"E25.7")])],"isStart":false});
            extrude(context, id + "F17", {"entities" : qUnion([Q0, Q1, Q2]), "endBound" : BoundingType.UP_TO_SURFACE, "endBoundEntityFace" : qUnion([Q3]), "depth" : 25 * mm});
        }
    });
